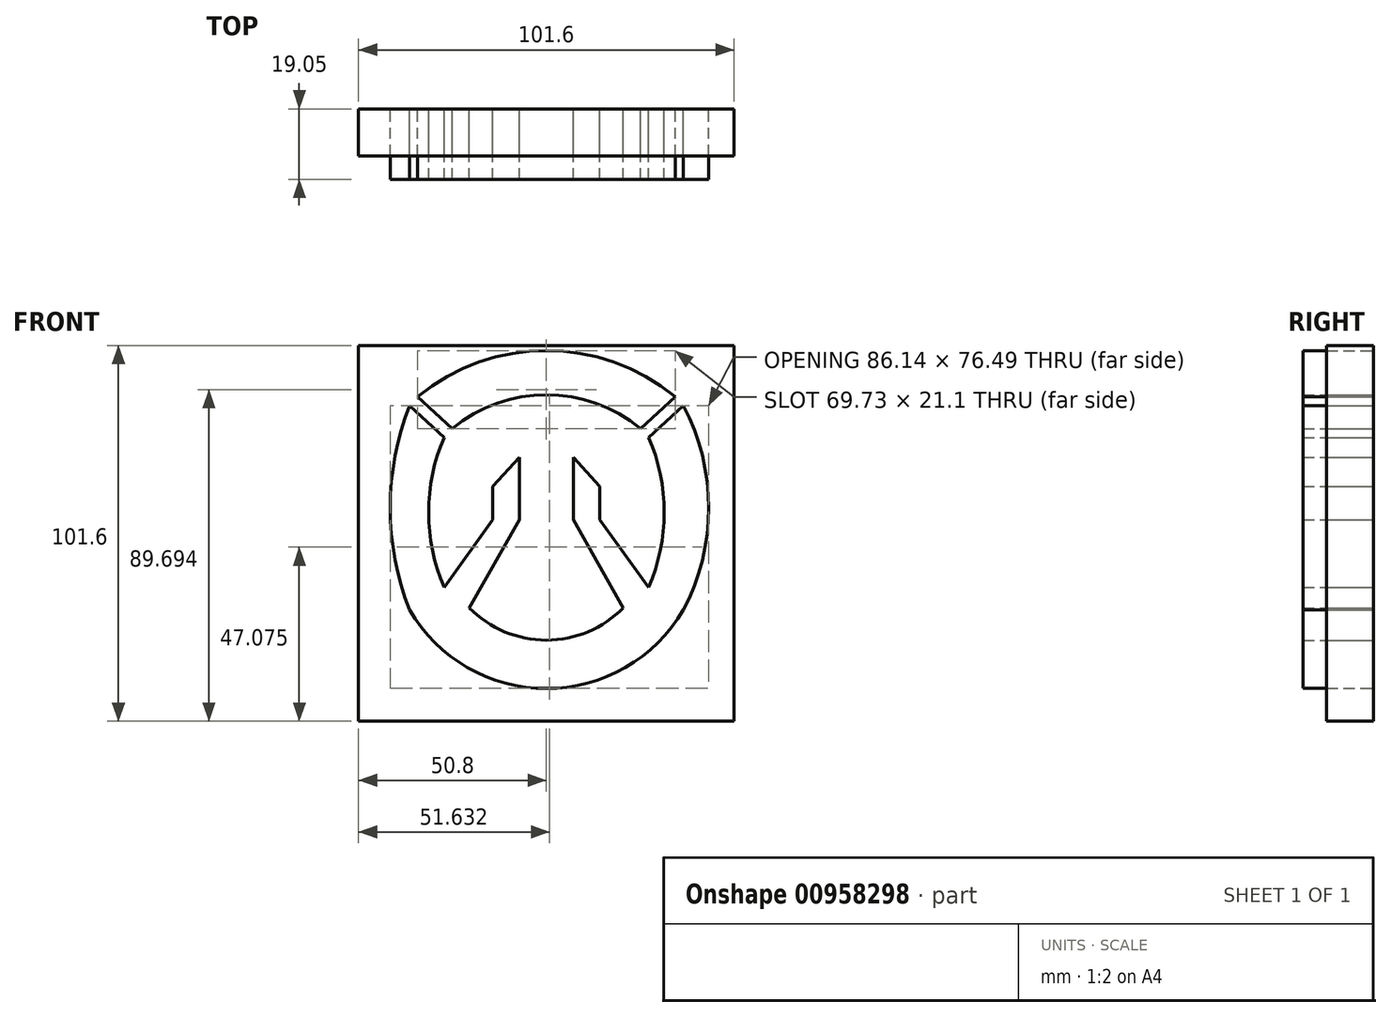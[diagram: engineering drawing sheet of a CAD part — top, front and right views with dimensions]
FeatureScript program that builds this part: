
annotation { "Feature Type Name" : "Feature", "Feature Type Description" : "" }
export const myFeature = defineFeature(function(context is Context, id is Id, definition is map)
    precondition{}
    {
        {
            var Q0;
            Q0=qCreatedBy(makeId("Front.planeOp"),FACE);
            var sketch = newSketch(context, id + "F0", { "sketchPlane" : qUnion([Q0])});
            skLineSegment(sketch, "E0.MirrorCS", {"start": v(34.87, 36.93) * mm, "end": v(25.5, 28.34) * mm});
            skLineSegment(sketch, "E1.MirrorCS", {"start": v(-34.87, 36.93) * mm, "end": v(-25.5, 28.34) * mm});
            skArc(sketch, "E2", {"start": v(25.5, 28.34) * mm, "mid": v(0, 37.47) * mm, "end": v(-25.5, 28.34) * mm});
            skArc(sketch, "E3", {"start": v(34.87, 36.93) * mm, "mid": v(0, 49.44) * mm, "end": v(-34.87, 36.93) * mm});
            skLineSegment(sketch, "E4.MirrorCS", {"start": v(37.03, 34.52) * mm, "end": v(27.67, 25.94) * mm});
            skLineSegment(sketch, "E5.MirrorCS", {"start": v(-37.03, 34.52) * mm, "end": v(-27.67, 25.94) * mm});
            skArc(sketch, "E6", {"start": v(37.03, -20.77) * mm, "mid": v(43.9, 6.88) * mm, "end": v(37.03, 34.52) * mm});
            skArc(sketch, "E7", {"start": v(-37.03, -20.77) * mm, "mid": v(0, -41.97) * mm, "end": v(37.03, -20.77) * mm});
            skArc(sketch, "E8", {"start": v(-37.03, 34.52) * mm, "mid": v(-42.24, 6.88) * mm, "end": v(-37.03, -20.77) * mm});
            skArc(sketch, "E9", {"start": v(27.67, -14.6) * mm, "mid": v(31.85, 5.67) * mm, "end": v(27.67, 25.94) * mm});
            skArc(sketch, "E10.MirrorCS", {"start": v(-27.67, -14.6) * mm, "mid": v(-31.85, 5.67) * mm, "end": v(-27.67, 25.94) * mm});
            skLineSegment(sketch, "E11", {"start": v(-27.67, -14.6) * mm, "end": v(-14.46, 3.71) * mm});
            skLineSegment(sketch, "E12", {"start": v(-14.46, 3.71) * mm, "end": v(-14.46, 12.74) * mm});
            skLineSegment(sketch, "E13", {"start": v(-14.46, 12.74) * mm, "end": v(-7.31, 20.53) * mm});
            skLineSegment(sketch, "E14", {"start": v(-7.31, 20.53) * mm, "end": v(-7.31, 3.71) * mm});
            skLineSegment(sketch, "E15", {"start": v(-7.31, 3.71) * mm, "end": v(-20.83, -20.17) * mm});
            skLineSegment(sketch, "E16.MirrorCS", {"start": v(7.31, 20.53) * mm, "end": v(7.31, 3.71) * mm});
            skLineSegment(sketch, "E17.MirrorCS", {"start": v(14.46, 12.74) * mm, "end": v(7.31, 20.53) * mm});
            skLineSegment(sketch, "E18.MirrorCS", {"start": v(14.46, 3.71) * mm, "end": v(14.46, 12.74) * mm});
            skLineSegment(sketch, "E19.MirrorCS", {"start": v(7.31, 3.71) * mm, "end": v(20.83, -20.17) * mm});
            skLineSegment(sketch, "E20.MirrorCS", {"start": v(27.67, -14.6) * mm, "end": v(14.46, 3.71) * mm});
            skArc(sketch, "E21", {"start": v(-20.83, -20.17) * mm, "mid": v(0, -28.9) * mm, "end": v(20.83, -20.17) * mm});
            skPoint(sketch, "E22.top.end.orphan", {"position": v(32.35, 30.23) * mm});
            skLineSegment(sketch, "E23.bottom", {"start": v(50.8, 50.8) * mm, "end": v(-50.8, 50.8) * mm});
            skLineSegment(sketch, "E23.top", {"start": v(50.8, -50.8) * mm, "end": v(-50.8, -50.8) * mm});
            skLineSegment(sketch, "E23.left", {"start": v(50.8, 50.8) * mm, "end": v(50.8, -50.8) * mm});
            skLineSegment(sketch, "E23.right", {"start": v(-50.8, 50.8) * mm, "end": v(-50.8, -50.8) * mm});
            skPoint(sketch, "E23.middle", {"position": v(0, 0) * mm});
            skSolve(sketch);
        }
        {
            var Q0;
            {var subQ0=sQuery(id+"F0.wireOp",EDGE,"E2");Q0=makeQuery(id+"F0.imprint","IMPRINT",FACE,{"disambiguationData":[TD([[makeQuery(id+"F0.imprint","IMPRINT",EDGE,{"derivedFrom":subQ0}),-1.0]])]});}
            var Q1;
            {var subQ3=sQuery(id+"F0.wireOp",EDGE,"E6");Q1=makeQuery(id+"F0.imprint","IMPRINT",FACE,{"disambiguationData":[TD([[makeQuery(id+"F0.imprint","IMPRINT",EDGE,{"derivedFrom":subQ3}),1.0]])]});}
            extrude(context, id + "F1", {"entities" : qUnion([Q0, Q1]), "depth" : 19.05 * mm, "offsetDistance" : 25.4 * mm});
        }
        {
            var Q0;
            Q0 = qSketchRegion(id + "F0", true);
            extrude(context, id + "F2", {"entities" : qUnion([Q0]), "depth" : 12.7 * mm, "offsetDistance" : 25.4 * mm});
        }
    });
